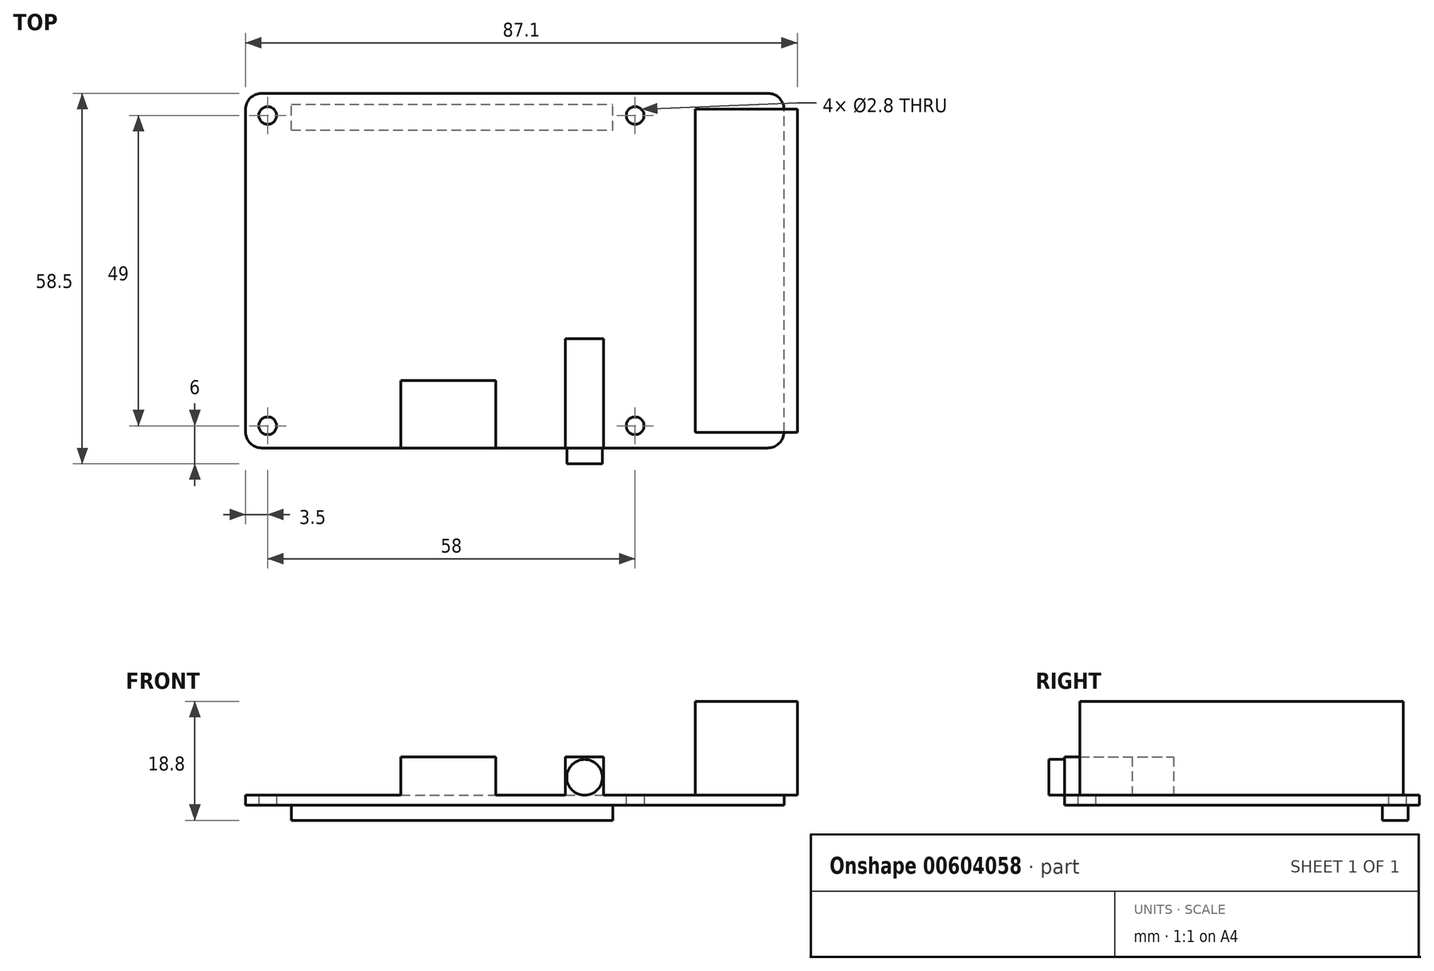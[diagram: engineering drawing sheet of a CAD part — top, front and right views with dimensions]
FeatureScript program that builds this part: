
annotation { "Feature Type Name" : "Feature", "Feature Type Description" : "" }
export const myFeature = defineFeature(function(context is Context, id is Id, definition is map)
    precondition{}
    {
        {
            var Q0;
            Q0=qCreatedBy(makeId("Top.planeOp"),FACE);
            var sketch = newSketch(context, id + "F0", { "sketchPlane" : qUnion([Q0])});
            skLineSegment(sketch, "E0.bottom", {"start": v(2.54, 0) * mm, "end": v(82.46, 0) * mm});
            skLineSegment(sketch, "E0.top", {"start": v(2.54, 56) * mm, "end": v(82.46, 56) * mm});
            skLineSegment(sketch, "E0.left", {"start": v(0, 2.54) * mm, "end": v(0, 53.46) * mm});
            skLineSegment(sketch, "E0.right", {"start": v(85, 2.54) * mm, "end": v(85, 53.46) * mm});
            skPoint(sketch, "E1.visualSharp", {"position": v(0, 56) * mm});
            skArc(sketch, "E1.filletArc", {"start": v(2.54, 56) * mm, "mid": v(0.74, 55.26) * mm, "end": v(0, 53.46) * mm});
            skPoint(sketch, "E2.visualSharp", {"position": v(85, 56) * mm});
            skArc(sketch, "E2.filletArc", {"start": v(85, 53.46) * mm, "mid": v(84.26, 55.26) * mm, "end": v(82.46, 56) * mm});
            skPoint(sketch, "E3.visualSharp", {"position": v(85, 0) * mm});
            skArc(sketch, "E3.filletArc", {"start": v(82.46, 0) * mm, "mid": v(84.26, 0.74) * mm, "end": v(85, 2.54) * mm});
            skPoint(sketch, "E4.visualSharp", {"position": v(0, 0) * mm});
            skArc(sketch, "E4.filletArc", {"start": v(0, 2.54) * mm, "mid": v(0.74, 0.74) * mm, "end": v(2.54, 0) * mm});
            skCircle(sketch, "E5", {"center": v(3.5, 52.5) * mm, "radius": 1.4 * mm});
            skCircle(sketch, "E6", {"center": v(61.5, 52.5) * mm, "radius": 1.4 * mm});
            skCircle(sketch, "E7", {"center": v(3.5, 3.5) * mm, "radius": 1.4 * mm});
            skCircle(sketch, "E8", {"center": v(61.5, 3.5) * mm, "radius": 1.4 * mm});
            skSolve(sketch);
        }
        {
            var Q0;
            Q0=makeQuery(id+"F0.imprint","IMPRINT",FACE,{"disambiguationData":[TD([[makeQuery(id+"F0.imprint","IMPRINT",EDGE,{"derivedFrom":sQuery(id+"F0.wireOp",EDGE,"E0.bottom")}),1.0]])]});
            extrude(context, id + "F1", {"entities" : qUnion([Q0]), "depth" : 1.6 * mm, "offsetDistance" : 25.4 * mm});
        }
        {
            var Q0;
            Q0=makeQuery(id+"F1.opExtrude","CAP_FACE",FACE,{"disambiguationData":[OSD([sQuery(id+"F0.wireOp",EDGE,"E0.bottom"),sQuery(id+"F0.wireOp",EDGE,"E0.top"),sQuery(id+"F0.wireOp",EDGE,"E0.left"),sQuery(id+"F0.wireOp",EDGE,"E0.right"),sQuery(id+"F0.wireOp",EDGE,"E1.filletArc"),sQuery(id+"F0.wireOp",EDGE,"E2.filletArc"),sQuery(id+"F0.wireOp",EDGE,"E3.filletArc"),sQuery(id+"F0.wireOp",EDGE,"E4.filletArc"),sQuery(id+"F0.wireOp",EDGE,"E5"),sQuery(id+"F0.wireOp",EDGE,"E6"),sQuery(id+"F0.wireOp",EDGE,"E7"),sQuery(id+"F0.wireOp",EDGE,"E8")])],"isStart":false});
            var sketch = newSketch(context, id + "F2", { "sketchPlane" : qUnion([Q0])});
            skLineSegment(sketch, "E9.0.0", {"start": v(82.46, 56) * mm, "end": v(2.54, 56) * mm});
            skArc(sketch, "E9.0.1", {"start": v(2.54, 56) * mm, "mid": v(0.74, 55.26) * mm, "end": v(0, 53.46) * mm});
            skLineSegment(sketch, "E9.0.2", {"start": v(0, 53.46) * mm, "end": v(0, 2.54) * mm});
            skArc(sketch, "E9.0.3", {"start": v(0, 2.54) * mm, "mid": v(0.74, 0.74) * mm, "end": v(2.54, 0) * mm});
            skLineSegment(sketch, "E9.0.4", {"start": v(2.54, 0) * mm, "end": v(82.46, 0) * mm});
            skArc(sketch, "E9.0.5", {"start": v(82.46, 0) * mm, "mid": v(84.26, 0.74) * mm, "end": v(85, 2.54) * mm});
            skLineSegment(sketch, "E9.0.6", {"start": v(85, 2.54) * mm, "end": v(85, 53.46) * mm});
            skArc(sketch, "E9.0.7", {"start": v(85, 53.46) * mm, "mid": v(84.26, 55.26) * mm, "end": v(82.46, 56) * mm});
            skLineSegment(sketch, "E10.bottom", {"start": v(70.97, 53.5) * mm, "end": v(87.1, 53.5) * mm});
            skLineSegment(sketch, "E10.top", {"start": v(70.97, 2.43) * mm, "end": v(87.1, 2.43) * mm});
            skLineSegment(sketch, "E10.left", {"start": v(70.97, 53.5) * mm, "end": v(70.97, 2.43) * mm});
            skLineSegment(sketch, "E10.right", {"start": v(87.1, 53.5) * mm, "end": v(87.1, 2.43) * mm});
            skSolve(sketch);
        }
        {
            var Q0;
            {var subQ1=sQuery(id+"F2.wireOp",EDGE,"E9.0.6");Q0=makeQuery(id+"F2.imprint","IMPRINT",FACE,{"disambiguationData":[TD([[makeQuery(id+"F2.imprint","IMPRINT",EDGE,{"derivedFrom":subQ1}),-1.0]])]});}
            var Q1;
            {var subQ4=sQuery(id+"F2.wireOp",EDGE,"E9.0.6");Q1=makeQuery(id+"F2.imprint","IMPRINT",FACE,{"disambiguationData":[TD([[makeQuery(id+"F2.imprint","IMPRINT",EDGE,{"derivedFrom":subQ4}),1.0]])]});}
            extrude(context, id + "F3", {"entities" : qUnion([Q0, Q1]), "operationType" : NewBodyOperationType.ADD, "depth" : 14.8 * mm, "offsetDistance" : 25.4 * mm});
        }
        {
            var Q0;
            Q0=makeQuery(id+"F1.opExtrude","CAP_FACE",FACE,{"disambiguationData":[OSD([sQuery(id+"F0.wireOp",EDGE,"E0.bottom"),sQuery(id+"F0.wireOp",EDGE,"E0.top"),sQuery(id+"F0.wireOp",EDGE,"E0.left"),sQuery(id+"F0.wireOp",EDGE,"E0.right"),sQuery(id+"F0.wireOp",EDGE,"E1.filletArc"),sQuery(id+"F0.wireOp",EDGE,"E2.filletArc"),sQuery(id+"F0.wireOp",EDGE,"E3.filletArc"),sQuery(id+"F0.wireOp",EDGE,"E4.filletArc"),sQuery(id+"F0.wireOp",EDGE,"E5"),sQuery(id+"F0.wireOp",EDGE,"E6"),sQuery(id+"F0.wireOp",EDGE,"E7"),sQuery(id+"F0.wireOp",EDGE,"E8")])],"isStart":true});
            var sketch = newSketch(context, id + "F4", { "sketchPlane" : qUnion([Q0])});
            skLineSegment(sketch, "E11.bottom", {"start": v(7.23, -50.18) * mm, "end": v(57.98, -50.18) * mm});
            skLineSegment(sketch, "E11.top", {"start": v(7.23, -54.24) * mm, "end": v(57.98, -54.24) * mm});
            skLineSegment(sketch, "E11.left", {"start": v(7.23, -50.18) * mm, "end": v(7.23, -54.24) * mm});
            skLineSegment(sketch, "E11.right", {"start": v(57.98, -50.18) * mm, "end": v(57.98, -54.24) * mm});
            skSolve(sketch);
        }
        {
            var Q0;
            Q0=makeQuery(id+"F4.imprint","IMPRINT",FACE,{"disambiguationData":[TD([[makeQuery(id+"F4.imprint","IMPRINT",EDGE,{"derivedFrom":sQuery(id+"F4.wireOp",EDGE,"E11.bottom")}),-1.0]])]});
            extrude(context, id + "F5", {"entities" : qUnion([Q0]), "operationType" : NewBodyOperationType.ADD, "depth" : 2.4 * mm, "offsetDistance" : 25.4 * mm});
        }
        {
            var Q0;
            Q0=makeQuery(id+"F1.opExtrude","CAP_FACE",FACE,{"disambiguationData":[OSD([sQuery(id+"F0.wireOp",EDGE,"E0.bottom"),sQuery(id+"F0.wireOp",EDGE,"E0.top"),sQuery(id+"F0.wireOp",EDGE,"E0.left"),sQuery(id+"F0.wireOp",EDGE,"E0.right"),sQuery(id+"F0.wireOp",EDGE,"E1.filletArc"),sQuery(id+"F0.wireOp",EDGE,"E2.filletArc"),sQuery(id+"F0.wireOp",EDGE,"E3.filletArc"),sQuery(id+"F0.wireOp",EDGE,"E4.filletArc"),sQuery(id+"F0.wireOp",EDGE,"E5"),sQuery(id+"F0.wireOp",EDGE,"E6"),sQuery(id+"F0.wireOp",EDGE,"E7"),sQuery(id+"F0.wireOp",EDGE,"E8")])],"isStart":false});
            var sketch = newSketch(context, id + "F6", { "sketchPlane" : qUnion([Q0])});
            skLineSegment(sketch, "E12.bottom", {"start": v(24.5, 0) * mm, "end": v(39.5, 0) * mm});
            skLineSegment(sketch, "E12.top", {"start": v(24.5, 10.66) * mm, "end": v(39.5, 10.66) * mm});
            skLineSegment(sketch, "E12.left", {"start": v(24.5, 0) * mm, "end": v(24.5, 10.66) * mm});
            skLineSegment(sketch, "E12.right", {"start": v(39.5, 0) * mm, "end": v(39.5, 10.66) * mm});
            skLineSegment(sketch, "E13.bottom", {"start": v(50.5, 0) * mm, "end": v(56.5, 0) * mm});
            skLineSegment(sketch, "E13.top", {"start": v(50.5, 17.25) * mm, "end": v(56.5, 17.25) * mm});
            skLineSegment(sketch, "E13.left", {"start": v(50.5, 0) * mm, "end": v(50.5, 17.25) * mm});
            skLineSegment(sketch, "E13.right", {"start": v(56.5, 0) * mm, "end": v(56.5, 17.25) * mm});
            skSolve(sketch);
        }
        {
            var Q0;
            Q0=makeQuery(id+"F6.imprint","IMPRINT",FACE,{"disambiguationData":[TD([[makeQuery(id+"F6.imprint","IMPRINT",EDGE,{"derivedFrom":sQuery(id+"F6.wireOp",EDGE,"E12.bottom")}),1.0]])]});
            var Q1;
            Q1=makeQuery(id+"F6.imprint","IMPRINT",FACE,{"disambiguationData":[TD([[makeQuery(id+"F6.imprint","IMPRINT",EDGE,{"derivedFrom":sQuery(id+"F6.wireOp",EDGE,"E13.bottom")}),1.0]])]});
            extrude(context, id + "F7", {"entities" : qUnion([Q0, Q1]), "operationType" : NewBodyOperationType.ADD, "depth" : 6 * mm, "offsetDistance" : 25.4 * mm});
        }
        {
            var Q0;
            Q0=makeQuery(id+"F7.boolean.opBoolean","MERGE",FACE,{"derivedFrom":[makeQuery(id+"F1.opExtrude","SWEPT_FACE",FACE,{"disambiguationData":[OSD([sQuery(id+"F0.wireOp",EDGE,"E0.bottom")])]}),makeQuery(id+"F7.opExtrude","SWEPT_FACE",FACE,{"disambiguationData":[OSD([sQuery(id+"F6.wireOp",EDGE,"E12.bottom")])]}),makeQuery(id+"F7.opExtrude","SWEPT_FACE",FACE,{"disambiguationData":[OSD([sQuery(id+"F6.wireOp",EDGE,"E13.bottom")])]})]});
            var sketch = newSketch(context, id + "F8", { "sketchPlane" : qUnion([Q0])});
            skCircle(sketch, "E14", {"center": v(53.52, 4.38) * mm, "radius": 2.82 * mm});
            skSolve(sketch);
        }
        {
            var Q0;
            Q0=makeQuery(id+"F8.imprint","IMPRINT",FACE,{"disambiguationData":[TD([[makeQuery(id+"F8.imprint","IMPRINT",EDGE,{"derivedFrom":sQuery(id+"F8.wireOp",EDGE,"E14")}),1.0]])]});
            extrude(context, id + "F9", {"entities" : qUnion([Q0]), "operationType" : NewBodyOperationType.ADD, "depth" : 2.5 * mm, "offsetDistance" : 25.4 * mm});
        }
    });
